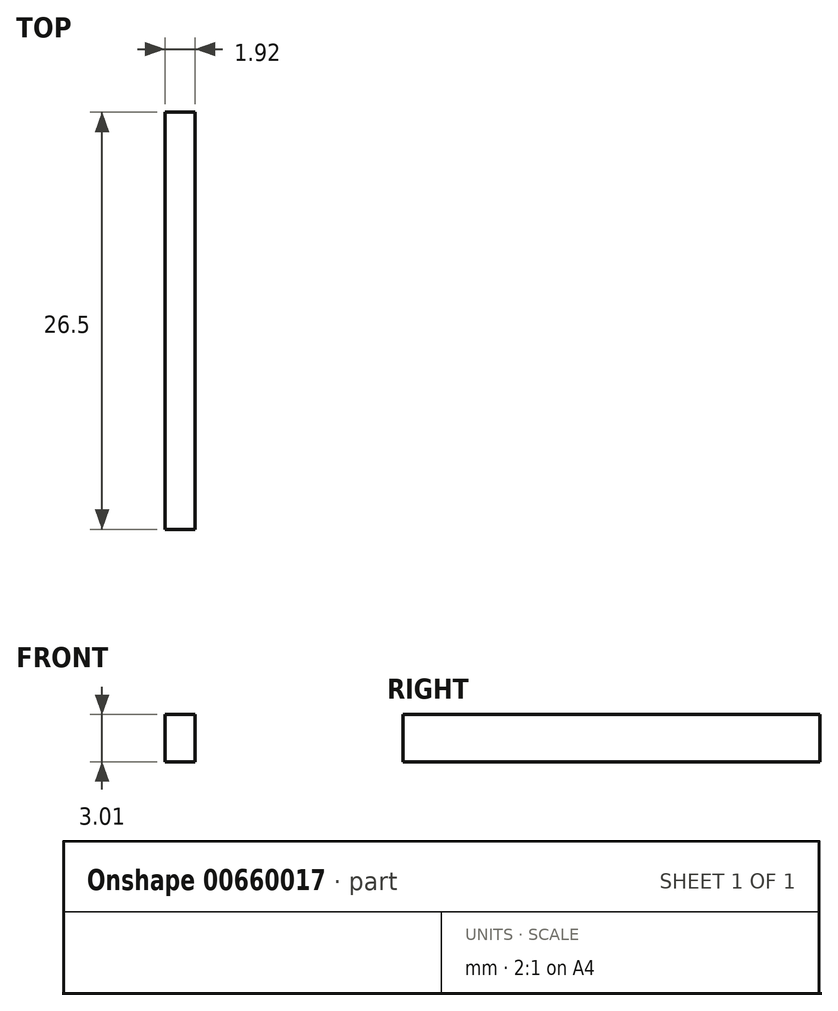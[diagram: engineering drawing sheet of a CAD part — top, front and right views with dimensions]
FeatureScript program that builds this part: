
annotation { "Feature Type Name" : "Feature", "Feature Type Description" : "" }
export const myFeature = defineFeature(function(context is Context, id is Id, definition is map)
    precondition{}
    {
        {
            var Q0;
            Q0=qCreatedBy(makeId("Front.planeOp"),FACE);
            var sketch = newSketch(context, id + "F0", { "sketchPlane" : qUnion([Q0])});
            skFitSpline(sketch, "E0", {"points": [v(44.37, 23.31) * mm, v(71.16, -16.2) * mm, v(43.13, -65.56) * mm, v(-65, -40.4) * mm, v(-30, 46) * mm, v(41.77, 19.62) * mm, v(41.77, 30.28) * mm, v(0, 52.3) * mm, v(-26.04, 59.95) * mm, v(-43.82, 55.99) * mm], "startDerivative": vector(330.2, -325.28) * mm, "endDerivative": vector(-259.73, -90.53) * mm});
            skSolve(sketch);
        }
        {
            var Q0;
            Q0 = qSketchRegion(id + "F0", true);
            var Q1;
            Q1=sQuery(id+"F0.wireOp",EDGE,"E0");
            extrude(context, id + "F1", {"entities" : qUnion([Q0]), "bodyType" : ToolBodyType.SURFACE, "surfaceEntities" : qUnion([Q1]), "depth" : 25 * mm, "offsetDistance" : 25 * mm});
        }
        {
            var Q0;
            Q0=qCreatedBy(makeId("Front.planeOp"),FACE);
            var sketch = newSketch(context, id + "F2", { "sketchPlane" : qUnion([Q0])});
            skLineSegment(sketch, "E1.bottom", {"start": v(45.19, 24.54) * mm, "end": v(43.27, 24.54) * mm});
            skLineSegment(sketch, "E1.top", {"start": v(45.19, 21.53) * mm, "end": v(43.27, 21.53) * mm});
            skLineSegment(sketch, "E1.left", {"start": v(45.19, 24.54) * mm, "end": v(45.19, 21.53) * mm});
            skLineSegment(sketch, "E1.right", {"start": v(43.27, 24.54) * mm, "end": v(43.27, 21.53) * mm});
            skSolve(sketch);
        }
        {
            var Q0;
            Q0 = qSketchRegion(id + "F2", true);
            extrude(context, id + "F3", {"entities" : qUnion([Q0]), "depth" : 25 * mm, "offsetDistance" : 25 * mm});
        }
        {
            var Q0;
            Q0=makeQuery(id+"F3.opExtrude","CAP_FACE",FACE,{"disambiguationData":[OSD([sQuery(id+"F2.wireOp",EDGE,"E1.bottom"),sQuery(id+"F2.wireOp",EDGE,"E1.top"),sQuery(id+"F2.wireOp",EDGE,"E1.left"),sQuery(id+"F2.wireOp",EDGE,"E1.right")])],"isStart":true});
            extrude(context, id + "F4", {"entities" : qUnion([Q0]), "operationType" : NewBodyOperationType.ADD, "depth" : 0.65 * mm, "offsetDistance" : 25 * mm});
        }
        {
            var Q0;
            Q0=makeQuery(id+"F3.opExtrude","CAP_FACE",FACE,{"disambiguationData":[OSD([sQuery(id+"F2.wireOp",EDGE,"E1.bottom"),sQuery(id+"F2.wireOp",EDGE,"E1.top"),sQuery(id+"F2.wireOp",EDGE,"E1.left"),sQuery(id+"F2.wireOp",EDGE,"E1.right")])],"isStart":false});
            extrude(context, id + "F5", {"entities" : qUnion([Q0]), "operationType" : NewBodyOperationType.ADD, "depth" : 0.85 * mm, "offsetDistance" : 25 * mm});
        }
    });
